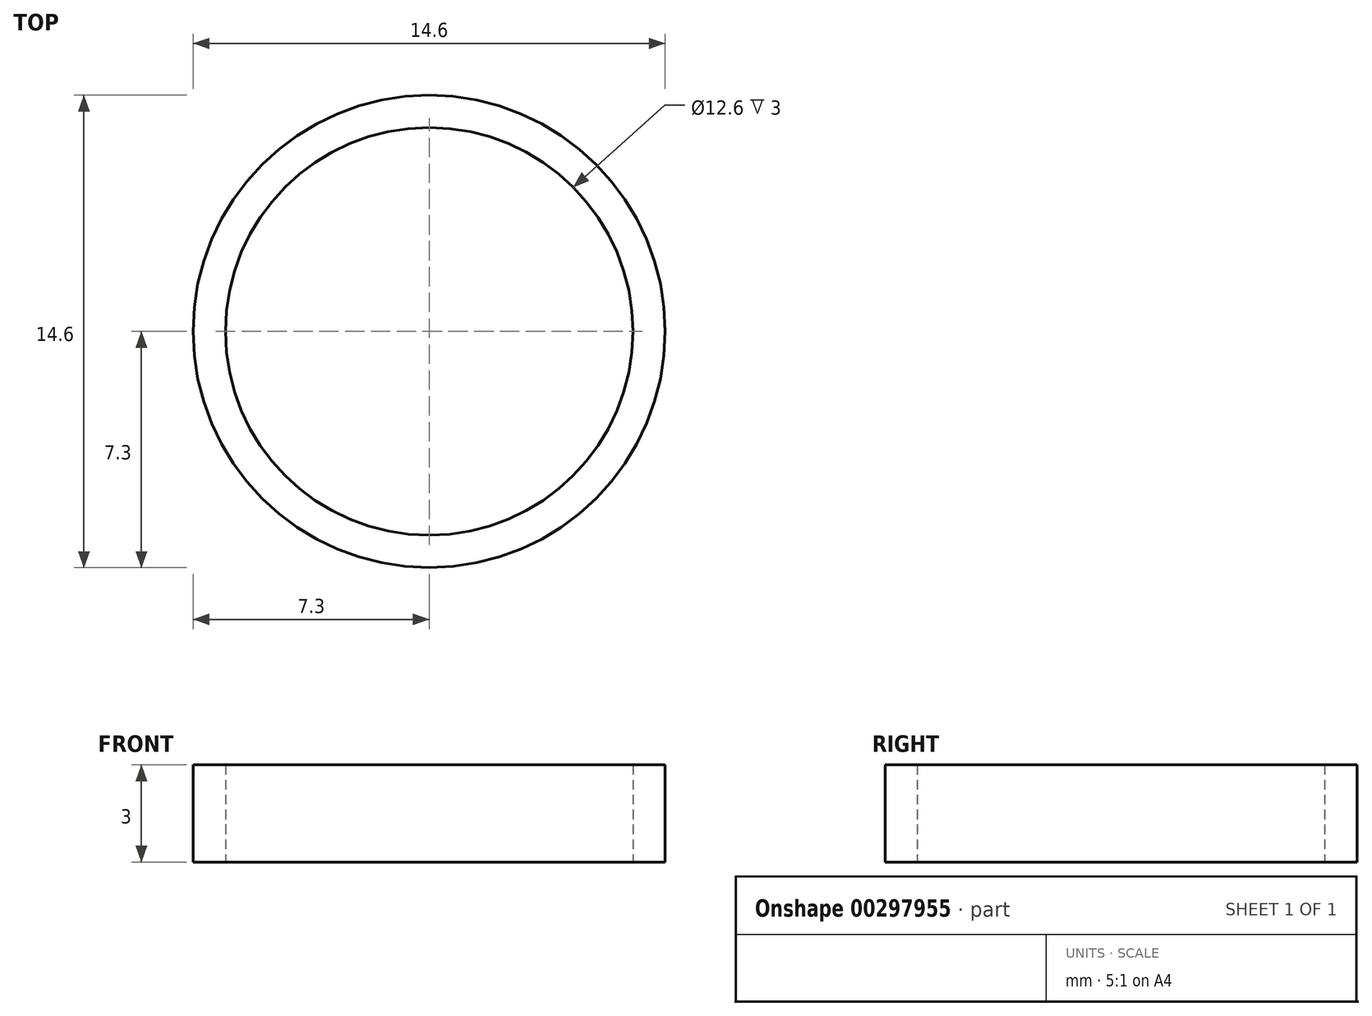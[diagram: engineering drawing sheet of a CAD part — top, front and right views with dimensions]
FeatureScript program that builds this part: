
annotation { "Feature Type Name" : "Feature", "Feature Type Description" : "" }
export const myFeature = defineFeature(function(context is Context, id is Id, definition is map)
    precondition{}
    {
        {
            var Q0;
            Q0=qCreatedBy(makeId("Top.planeOp"),FACE);
            var sketch = newSketch(context, id + "F0", { "sketchPlane" : qUnion([Q0])});
            skCircle(sketch, "E0", {"center": v(0, 0) * mm, "radius": 6.3 * mm});
            skCircle(sketch, "E1", {"center": v(0, 0) * mm, "radius": 7.3 * mm});
            skSolve(sketch);
        }
        {
            var Q0;
            Q0 = qSketchRegion(id + "F0", true);
            extrude(context, id + "F1", {"entities" : qUnion([Q0]), "depth" : 3 * mm});
        }
    });
